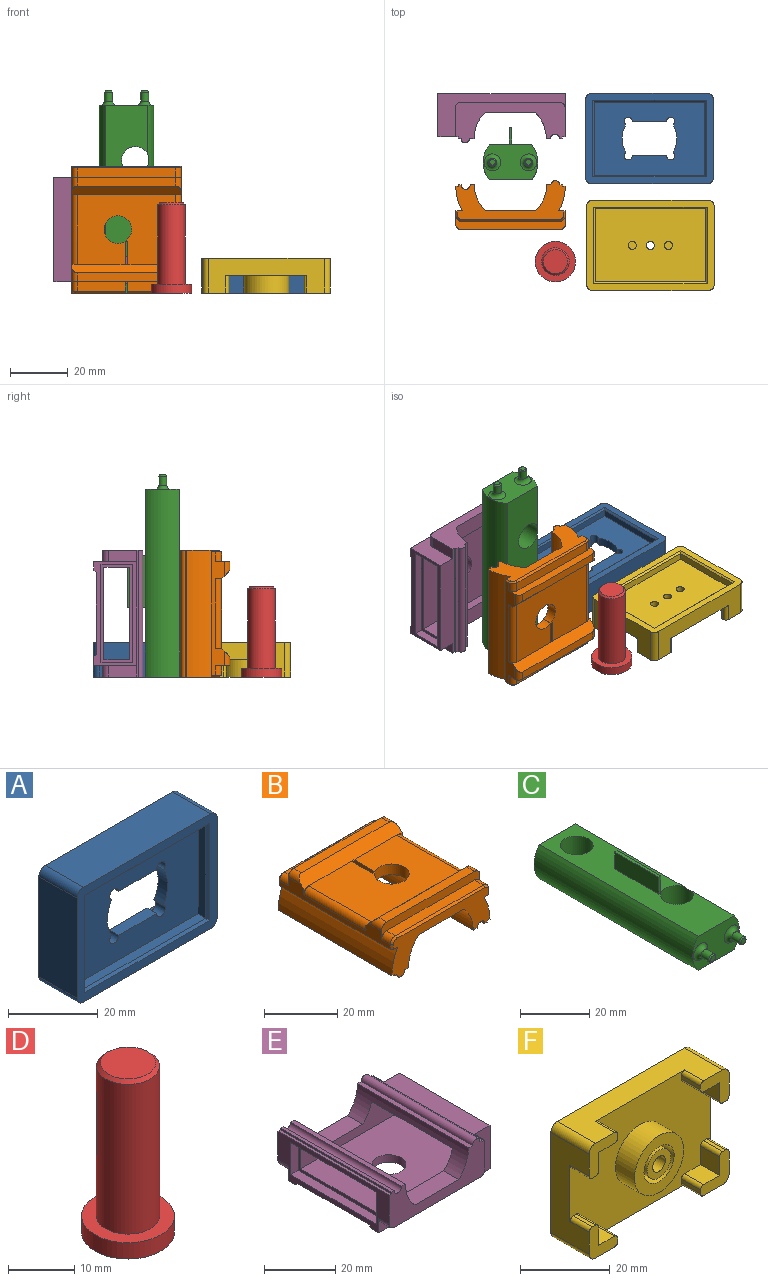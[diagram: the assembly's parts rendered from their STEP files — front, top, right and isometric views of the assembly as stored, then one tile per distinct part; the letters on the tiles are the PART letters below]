
ASSEMBLY  parts=6 mates=5
PART A: 32 faces, bbox 44.1x12x31.3 mm
  f0: plane 38.1x25.3mm, normal (0,1,0), area 736.2mm2, adj f1,f2,f3,f4,f5,f6,f7,f8
  f1: cylinder r=1.4mm len=3mm, axis (0,1,0), area 17.2mm2, adj f0,f2,f8,f9
  f2: plane 11.93x3mm, normal (0,0,-1), area 35.8mm2, adj f0,f1,f3,f9
  f3: cylinder r=1.4mm len=3mm, axis (0,1,0), area 17.2mm2, adj f0,f2,f4,f9
  f4: cylinder r=9.5mm len=9.7mm, axis (0,1,0), area 30.6mm2, adj f0,f3,f5,f9
  f5: cylinder r=1.4mm len=3mm, axis (0,1,0), area 17.2mm2, adj f0,f4,f6,f9
  f6: plane 11.93x3mm, normal (0,0,1), area 35.8mm2, adj f0,f5,f7,f9
  f7: cylinder r=1.4mm len=3mm, axis (0,1,0), area 17.2mm2, adj f0,f6,f8,f9
  f8: cylinder r=9.5mm len=9.7mm, axis (0,1,0), area 30.6mm2, adj f0,f1,f7,f9
  f9: plane 38.1x25.3mm, normal (0,-1,0), area 736.2mm2, adj f1,f2,f3,f4,f5,f6,f7,f8
  f10: plane 38.1x2.4mm, normal (0,0,-1), area 91.4mm2, adj f9,f11,f13,f25
  f11: plane 25.3x2.4mm, normal (1,0,0), area 60.7mm2, adj f9,f10,f12,f24
  f12: plane 38.1x2.4mm, normal (0,0,1), area 91.4mm2, adj f9,f11,f13,f26
  f13: plane 25.3x2.4mm, normal (-1,0,0), area 60.7mm2, adj f9,f10,f12,f27
  f14: plane 40.1x12mm, normal (0,0,1), area 481.2mm2, adj f18,f23,f28,f31
  f15: plane 27.3x12mm, normal (-1,0,0), area 327.6mm2, adj f18,f23,f28,f29
  f16: plane 40.1x12mm, normal (0,0,-1), area 481.2mm2, adj f18,f23,f29,f30
  f17: plane 27.3x12mm, normal (1,0,0), area 327.6mm2, adj f18,f23,f30,f31
  f18: plane 44.1x31.3mm, normal (0,-1,0), area 335.4mm2, adj f14,f15,f16,f17,f24,f25,f26,f27
  f19: plane 25.3x6mm, normal (1,0,0), area 151.8mm2, adj f0,f20,f22,f23
  f20: plane 38.1x6mm, normal (0,0,-1), area 228.6mm2, adj f0,f19,f21,f23
  f21: plane 25.3x6mm, normal (-1,0,0), area 151.8mm2, adj f0,f20,f22,f23
  f22: plane 38.1x6mm, normal (0,0,1), area 228.6mm2, adj f0,f19,f21,f23
  f23: plane 44.1x31.3mm, normal (0,1,0), area 413mm2, adj f14,f15,f16,f17,f19,f20,f21,f22
  f24: plane 26.5x0.6mm, normal (0.71,-0.71,0), area 22mm2, adj f11,f18,f25,f26
  f25: plane 39.3x0.6mm, normal (0,-0.71,-0.71), area 32.8mm2, adj f10,f18,f24,f27
  f26: plane 39.3x0.6mm, normal (0,-0.71,0.71), area 32.8mm2, adj f12,f18,f24,f27
  f27: plane 26.5x0.6mm, normal (-0.71,-0.71,0), area 22mm2, adj f13,f18,f25,f26
  f28: cylinder r=2mm len=12mm, axis (0,-1,0), area 37.7mm2, adj f14,f15,f18,f23
  f29: cylinder r=2mm len=12mm, axis (0,1,0), area 37.7mm2, adj f15,f16,f18,f23
  f30: cylinder r=2mm len=12mm, axis (0,-1,0), area 37.7mm2, adj f16,f17,f18,f23
  f31: cylinder r=2mm len=12mm, axis (0,1,0), area 37.7mm2, adj f14,f17,f18,f23
PART B: 62 faces, bbox 38x44x17 mm
  f0: plane 1.9x1.36mm, normal (0,1,0), area 0.7mm2, adj f18,f42,f61
  f1: plane 1.9x1.36mm, normal (0,-1,0), area 0.7mm2, adj f17,f41,f60
  f2: plane 16.5x3.4mm, normal (0,0,1), area 56.1mm2, adj f4,f36,f40,f49
  f3: plane 16.5x3.4mm, normal (0,0,1), area 56.1mm2, adj f5,f36,f39,f52
  f4: plane 18x3.6mm, normal (1,0,0), area 64.1mm2, adj f2,f6,f8,f30,f31,f35,f36,f49
  f5: plane 17.96x3.6mm, normal (-1,0,0), area 63.9mm2, adj f3,f6,f8,f9,f10,f35,f36,f52
  f6: plane 34x24.21mm, normal (0,0,1), area 744.1mm2, adj f4,f5,f10,f31,f41,f42,f60,f61
  f7: plane 34x3.4mm, normal (0,0,1), area 115.6mm2, adj f34,f47,f48,f57
  f8: plane 44x17.35mm, normal (0,0,-1), area 674.5mm2, adj f4,f5,f9,f10,f26,f27,f29,f30
  f9: plane 18.49x12mm, normal (0,1,0), area 111.8mm2, adj f5,f8,f11,f12,f13,f14,f15,f16
  f10: cylinder r=4.75mm len=9.5mm, axis (0,0,-1), area 107.3mm2, adj f5,f6,f8,f31
  f11: cylinder r=1.5mm len=44mm, axis (0,1,0), area 207.3mm2, adj f9,f12,f28,f29
  f12: plane 44x1mm, normal (0,0,-1), area 44mm2, adj f9,f11,f13,f29
  f13: plane 44x0.5mm, normal (1,0,0), area 22mm2, adj f9,f12,f14,f29
  f14: plane 44x0.99mm, normal (0,0,-1), area 43.7mm2, adj f9,f13,f15,f29
  f15: cylinder r=19mm len=44mm, axis (0,1,0), area 390.5mm2, adj f9,f14,f16,f29
  f16: plane 44x2.27mm, normal (0,0,-1), area 99.4mm2, adj f9,f15,f17,f29,f54,f55
  f17: plane 42.8x4.5mm, normal (1,0,0), area 102.4mm2, adj f1,f16,f32,f34,f36,f39,f41,f44
  f18: plane 42.8x4.5mm, normal (-1,0,0), area 102.4mm2, adj f0,f19,f34,f36,f38,f40,f42,f43
  f19: plane 44x2.27mm, normal (0,0,-1), area 99.4mm2, adj f18,f20,f29,f30,f51,f59
  f20: cylinder r=19mm len=44mm, axis (0,1,0), area 390.5mm2, adj f19,f21,f29,f30
  f21: plane 44x0.99mm, normal (0,0,-1), area 43.7mm2, adj f20,f22,f29,f30
  f22: plane 44x0.5mm, normal (-1,0,0), area 22mm2, adj f21,f23,f29,f30
  f23: plane 44x1mm, normal (0,0,-1), area 44mm2, adj f22,f24,f29,f30
  f24: cylinder r=1.5mm len=44mm, axis (0,1,0), area 207.3mm2, adj f23,f25,f29,f30
  f25: plane 44x1.5mm, normal (0,0,-1), area 66mm2, adj f24,f26,f29,f30
  f26: cylinder r=12.5mm len=44mm, axis (0,1,0), area 442.1mm2, adj f8,f25,f29,f30
  f27: cylinder r=12.5mm len=44mm, axis (0,1,0), area 442.1mm2, adj f8,f9,f28,f29
  f28: plane 44x1.5mm, normal (0,0,-1), area 66mm2, adj f9,f11,f27,f29
  f29: plane 37.99x13.5mm, normal (0,-1,0), area 233.8mm2, adj f8,f11,f12,f13,f14,f15,f16,f19
  f30: plane 18.49x13.5mm, normal (0,1,0), area 118.9mm2, adj f4,f8,f19,f20,f21,f22,f23,f24
  f31: plane 3.6x0.94mm, normal (0,1,0), area 3.4mm2, adj f4,f6,f8,f10
  f32: plane 1.9x1.36mm, normal (0,1,0), area 0.7mm2, adj f17,f41,f61
  f33: plane 34x3mm, normal (0,0,1), area 102mm2, adj f34,f45,f46,f61
  f34: plane 38x4.9mm, normal (0,-1,0), area 110.1mm2, adj f7,f17,f18,f33,f45,f46,f47,f48
  f35: plane 6x1mm, normal (0,0,-1), area 6mm2, adj f4,f5,f36,f60
  f36: plane 38x4.9mm, normal (0,1,0), area 110.2mm2, adj f2,f3,f4,f5,f17,f18,f35,f37
  f37: plane 34x3mm, normal (0,0,1), area 102mm2, adj f36,f43,f44,f60
  f38: plane 1.9x1.36mm, normal (0,-1,0), area 0.7mm2, adj f18,f42,f60
  f39: cylinder r=2mm len=3.4mm, axis (0,1,0), area 10.7mm2, adj f3,f17,f36,f53
  f40: cylinder r=2mm len=3.4mm, axis (0,-1,0), area 10.7mm2, adj f2,f18,f36,f50
  f41: cylinder r=2mm len=24.21mm, axis (0,1,0), area 75.5mm2, adj f1,f6,f17,f32,f60,f61
  f42: cylinder r=2mm len=24.21mm, axis (0,-1,0), area 75.5mm2, adj f0,f6,f18,f38,f60,f61
  f43: cylinder r=2mm len=5mm, axis (0,-1,0), area 11.7mm2, adj f18,f36,f37,f60
  f44: cylinder r=2mm len=5mm, axis (0,1,0), area 11.7mm2, adj f17,f36,f37,f60
  f45: cylinder r=2mm len=5mm, axis (0,-1,0), area 11.7mm2, adj f18,f33,f34,f61
  f46: cylinder r=2mm len=5mm, axis (0,1,0), area 11.7mm2, adj f17,f33,f34,f61
  f47: cylinder r=2mm len=3.4mm, axis (0,-1,0), area 10.7mm2, adj f7,f18,f34,f58
  f48: cylinder r=2mm len=3.4mm, axis (0,1,0), area 10.7mm2, adj f7,f17,f34,f56
  f49: plane 16.5x0.6mm, normal (0,0.71,0.71), area 14mm2, adj f2,f4,f30,f50
  f50: cone r=1.4mm half-angle=45deg, axis (0,-1,0), area 2.3mm2, adj f30,f40,f49,f51
  f51: plane 1.6x0.6mm, normal (-0.71,0.71,0), area 1.4mm2, adj f18,f19,f30,f50
  f52: plane 16.5x0.6mm, normal (0,0.71,0.71), area 14mm2, adj f3,f5,f9,f53
  f53: cone r=1.4mm half-angle=45deg, axis (0,-1,0), area 2.3mm2, adj f9,f39,f52,f54
  f54: plane 1.6x0.6mm, normal (0.71,0.71,0), area 1.4mm2, adj f9,f16,f17,f53
  f55: plane 1.6x0.6mm, normal (0.71,-0.71,0), area 1.4mm2, adj f16,f17,f29,f56
  f56: cone r=1.4mm half-angle=45deg, axis (0,1,0), area 2.3mm2, adj f29,f48,f55,f57
  f57: plane 34x0.6mm, normal (0,-0.71,0.71), area 28.8mm2, adj f7,f29,f56,f58
  f58: cone r=1.4mm half-angle=45deg, axis (0,1,0), area 2.3mm2, adj f29,f47,f57,f59
  f59: plane 1.6x0.6mm, normal (-0.71,-0.71,0), area 1.4mm2, adj f18,f19,f29,f58
  f60: plane 38x3mm, normal (0,-0.71,0.71), area 153.8mm2, adj f1,f4,f5,f6,f17,f18,f35,f37
  f61: plane 38x3mm, normal (0,0.71,0.71), area 153.7mm2, adj f0,f6,f17,f18,f32,f33,f41,f42
PART C: 21 faces, bbox 21.1x70x18 mm
  f0: plane 65x14.73mm, normal (0,0,1), area 798.8mm2, adj f1,f2,f4,f5,f6,f7,f8,f14
  f1: cylinder r=9.5mm len=65mm, axis (0,1,0), area 841.1mm2, adj f0,f3,f4,f5,f14
  f2: cylinder r=9.5mm len=65mm, axis (0,1,0), area 844.2mm2, adj f0,f3,f4,f5
  f3: plane 65x14.73mm, normal (0,0,-1), area 816.7mm2, adj f1,f2,f4,f5,f14,f15
  f4: plane 19x12mm, normal (0,-1,0), area 158.9mm2, adj f0,f1,f2,f3,f19,f20
  f5: plane 19x12mm, normal (0,1,0), area 211.8mm2, adj f0,f1,f2,f3
  f6: plane 6x1mm, normal (0,1,0), area 6mm2, adj f0,f7,f8,f9
  f7: plane 17.96x6mm, normal (-1,0,0), area 107.8mm2, adj f0,f6,f9,f16
  f8: plane 17.96x6mm, normal (1,0,0), area 107.8mm2, adj f0,f6,f9,f16
  f9: plane 17.96x1mm, normal (0,0,1), area 18mm2, adj f6,f7,f8,f16
  f10: cylinder r=1.4mm len=3.1mm, axis (0,1,0), area 27.3mm2, adj f18,f20
  f11: plane 2x2mm, normal (0,-1,0), area 3.1mm2, adj f18
  f12: cylinder r=1.4mm len=3.1mm, axis (0,1,0), area 27.3mm2, adj f17,f19
  f13: plane 2x2mm, normal (0,-1,0), area 3.1mm2, adj f17
  f14: cylinder r=4.75mm len=12mm, axis (0,0,-1), area 355.6mm2, adj f0,f1,f3
  f15: cylinder r=4.75mm len=12mm, axis (0,0,1), area 358.1mm2, adj f0,f3
  f16: plane 6x1mm, normal (0,-1,0), area 6mm2, adj f0,f7,f8,f9
  f17: cone r=1mm half-angle=45deg, axis (0,1,0), area 4.3mm2, adj f12,f13
  f18: cone r=1mm half-angle=45deg, axis (0,1,0), area 4.3mm2, adj f10,f11
  f19: torus R=2.9mm, axis (0,-1,0), area 28.8mm2, adj f4,f12
  f20: torus R=2.9mm, axis (0,-1,0), area 28.8mm2, adj f4,f10
PART D: 6 faces, bbox 14x14x31.2 mm
  f0: cylinder r=4.75mm len=27.6mm, axis (0,0,-1), area 823.7mm2, adj f3,f5
  f1: plane 8.3x8.3mm, normal (0,0,1), area 54.1mm2, adj f5
  f2: cylinder r=7mm len=14mm, axis (0,0,-1), area 131.9mm2, adj f3,f4
  f3: plane 14x14mm, normal (0,0,1), area 83.1mm2, adj f0,f2
  f4: plane 14x14mm, normal (0,0,-1), area 153.9mm2, adj f2
  f5: cone r=4.15mm half-angle=45deg, axis (0,0,-1), area 23.7mm2, adj f0,f1
PART E: 49 faces, bbox 44x44x17 mm
  f0: plane 38x14mm, normal (0,1,0), area 268.4mm2, adj f3,f5,f11,f12,f13,f17,f18,f19
  f1: plane 38x14mm, normal (0,-1,0), area 268.4mm2, adj f3,f4,f5,f11,f12,f16,f17,f18
  f2: plane 36x14.9mm, normal (1,0,0), area 136.3mm2, adj f3,f15,f26,f27,f28,f29,f30,f31
  f3: plane 44x7mm, normal (0,0,1), area 260mm2, adj f0,f1,f2,f22,f26,f28,f43,f44
  f4: plane 34x4mm, normal (0,0,-1), area 136mm2, adj f1,f28,f46,f48
  f5: plane 44x14.9mm, normal (-1,0,0), area 215.5mm2, adj f0,f1,f15,f21,f26,f27,f28,f29
  f6: plane 38x9mm, normal (0,1,0), area 212.6mm2, adj f8,f9,f10,f11,f12,f16,f34,f39
  f7: plane 38x9mm, normal (0,-1,0), area 212.6mm2, adj f8,f9,f10,f11,f12,f13,f34,f39
  f8: plane 38x32mm, normal (0,0,1), area 1145.1mm2, adj f6,f7,f14,f34,f39
  f9: plane 32x3.87mm, normal (0,0,-1), area 123.7mm2, adj f6,f7,f12,f39
  f10: plane 32x9.87mm, normal (0,0,-1), area 315.7mm2, adj f6,f7,f11,f34
  f11: cylinder r=12.5mm len=44mm, axis (0,1,0), area 217.5mm2, adj f0,f1,f6,f7,f10,f13,f16,f25
  f12: cylinder r=12.5mm len=44mm, axis (0,1,0), area 217.5mm2, adj f0,f1,f6,f7,f9,f13,f16,f17
  f13: plane 17.35x6mm, normal (0,0,1), area 104.1mm2, adj f0,f7,f11,f12
  f14: cylinder r=4.75mm len=9.5mm, axis (0,0,1), area 77.7mm2, adj f8,f15
  f15: plane 44x28.21mm, normal (0,0,-1), area 1170.2mm2, adj f2,f5,f14,f41,f42
  f16: plane 17.35x6mm, normal (0,0,1), area 104.1mm2, adj f1,f6,f11,f12
  f17: plane 44x1.5mm, normal (0,0,1), area 66mm2, adj f0,f1,f12,f18
  f18: cylinder r=1.5mm len=44mm, axis (0,1,0), area 207.3mm2, adj f0,f1,f17,f19
  f19: plane 44x1mm, normal (0,0,1), area 44mm2, adj f0,f1,f18,f20
  f20: plane 44x0.6mm, normal (-1,0,0), area 26.4mm2, adj f0,f1,f19,f21
  f21: plane 44x1mm, normal (0,0,1), area 44mm2, adj f0,f1,f5,f20
  f22: plane 44x0.6mm, normal (1,0,0), area 26.4mm2, adj f0,f1,f3,f23
  f23: plane 44x1mm, normal (0,0,1), area 44mm2, adj f0,f1,f22,f24
  f24: cylinder r=1.5mm len=44mm, axis (0,1,0), area 207.3mm2, adj f0,f1,f23,f25
  f25: plane 44x1.5mm, normal (0,0,1), area 66mm2, adj f0,f1,f11,f24
  f26: plane 44x14.9mm, normal (0,1,0), area 205.1mm2, adj f2,f3,f5,f27,f40,f44,f45,f47
  f27: plane 44x3mm, normal (0,0,-1), area 132mm2, adj f2,f5,f26,f42
  f28: plane 44x14.9mm, normal (0,-1,0), area 205.1mm2, adj f2,f3,f4,f5,f29,f43,f46,f48
  f29: plane 44x3mm, normal (0,0,-1), area 132mm2, adj f2,f5,f28,f41
  f30: plane 11x3mm, normal (0,1,0), area 33mm2, adj f2,f31,f33,f34
  f31: plane 34x3mm, normal (0,0,1), area 102mm2, adj f2,f30,f32,f34
  f32: plane 11x3mm, normal (0,-1,0), area 33mm2, adj f2,f31,f33,f34
  f33: plane 34x3mm, normal (0,0,-1), area 102mm2, adj f2,f30,f32,f34
  f34: plane 34x11mm, normal (1,0,0), area 86mm2, adj f6,f7,f8,f10,f30,f31,f32,f33
  f35: plane 11x3mm, normal (0,-1,0), area 33mm2, adj f5,f36,f38,f39
  f36: plane 34x3mm, normal (0,0,1), area 102mm2, adj f5,f35,f37,f39
  f37: plane 11x3mm, normal (0,1,0), area 33mm2, adj f5,f36,f38,f39
  f38: plane 34x3mm, normal (0,0,-1), area 102mm2, adj f5,f35,f37,f39
  f39: plane 34x11mm, normal (-1,0,0), area 86mm2, adj f6,f7,f8,f9,f35,f36,f37,f38
  f40: plane 34x4mm, normal (0,0,-1), area 136mm2, adj f0,f26,f45,f47
  f41: plane 44x0.9mm, normal (0,0.71,-0.71), area 55.8mm2, adj f2,f5,f15,f29
  f42: plane 44x0.9mm, normal (0,-0.71,-0.71), area 55.8mm2, adj f2,f5,f15,f27
  f43: plane 9.9x4mm, normal (1,0,0), area 39.6mm2, adj f1,f3,f28,f46
  f44: plane 9.9x4mm, normal (1,0,0), area 39.6mm2, adj f0,f3,f26,f45
  f45: cylinder r=2mm len=4mm, axis (0,-1,0), area 12.6mm2, adj f0,f26,f40,f44
  f46: cylinder r=2mm len=4mm, axis (0,-1,0), area 12.6mm2, adj f1,f4,f28,f43
  f47: cylinder r=2mm len=4mm, axis (0,-1,0), area 12.6mm2, adj f0,f5,f26,f40
  f48: cylinder r=2mm len=4mm, axis (0,-1,0), area 12.6mm2, adj f1,f4,f5,f28
PART F: 69 faces, bbox 44.1x12x31.3 mm
  f0: plane 9.5x9.5mm, normal (0,-1,0), area 26.7mm2, adj f17,f39
  f1: plane 44.1x31.3mm, normal (0,-1,0), area 1015.1mm2, adj f10,f11,f12,f13,f19,f20,f21,f22
  f2: cylinder r=1.4mm len=2.8mm, axis (0,-1,0), area 17.6mm2, adj f5,f16
  f3: cylinder r=1.4mm len=2.8mm, axis (0,-1,0), area 17.6mm2, adj f5,f15
  f4: cylinder r=2mm len=6mm, axis (0,-1,0), area 75.4mm2, adj f18,f47
  f5: plane 38.1x25.3mm, normal (0,1,0), area 945.5mm2, adj f2,f3,f6,f7,f8,f9,f46
  f6: plane 25.3x2.4mm, normal (-1,0,0), area 60.7mm2, adj f5,f7,f9,f44
  f7: plane 38.1x2.4mm, normal (0,0,-1), area 91.4mm2, adj f5,f6,f8,f42
  f8: plane 25.3x2.4mm, normal (1,0,0), area 60.7mm2, adj f5,f7,f9,f43
  f9: plane 38.1x2.4mm, normal (0,0,1), area 91.4mm2, adj f5,f6,f8,f45
  f10: plane 27.3x12mm, normal (-1,0,0), area 235.8mm2, adj f1,f14,f28,f33,f48,f50,f58,f68
  f11: plane 40.1x12mm, normal (0,0,-1), area 312.6mm2, adj f1,f14,f33,f38,f50,f51,f55,f57
  f12: plane 27.3x12mm, normal (1,0,0), area 235.8mm2, adj f1,f14,f23,f38,f49,f51,f54,f64
  f13: plane 40.1x12mm, normal (0,0,1), area 312.6mm2, adj f1,f14,f23,f28,f48,f49,f61,f65
  f14: plane 44.1x31.3mm, normal (0,1,0), area 335.4mm2, adj f10,f11,f12,f13,f42,f43,f44,f45
  f15: plane 2.8x2.8mm, normal (0,1,0), area 6.2mm2, adj f3
  f16: plane 2.8x2.8mm, normal (0,1,0), area 6.2mm2, adj f2
  f17: cylinder r=3.75mm len=7.5mm, axis (0,1,0), area 141.4mm2, adj f0,f18
  f18: plane 7.5x7.5mm, normal (0,-1,0), area 31.6mm2, adj f4,f17
  f19: plane 6x1mm, normal (-1,0,0), area 6mm2, adj f1,f23,f61,f62
  f20: plane 6x5mm, normal (0,0,-1), area 30mm2, adj f1,f21,f23,f62
  f21: plane 6x5mm, normal (-1,0,0), area 30mm2, adj f1,f20,f23,f63
  f22: plane 6x1mm, normal (0,0,-1), area 6mm2, adj f1,f23,f63,f64
  f23: plane 9x9mm, normal (0,-1,0), area 43.3mm2, adj f12,f13,f19,f20,f21,f22,f49,f61
  f24: plane 6x1mm, normal (0,0,-1), area 6mm2, adj f1,f28,f67,f68
  f25: plane 6x5mm, normal (1,0,0), area 30mm2, adj f1,f26,f28,f67
  f26: plane 6x5mm, normal (0,0,-1), area 30mm2, adj f1,f25,f28,f66
  f27: plane 6x1mm, normal (1,0,0), area 6mm2, adj f1,f28,f65,f66
  f28: plane 9x9mm, normal (0,-1,0), area 43.3mm2, adj f10,f13,f24,f25,f26,f27,f48,f65
  f29: plane 6x1mm, normal (1,0,0), area 6mm2, adj f1,f33,f57,f60
  f30: plane 6x5mm, normal (0,0,1), area 30mm2, adj f1,f31,f33,f60
  f31: plane 6x5mm, normal (1,0,0), area 30mm2, adj f1,f30,f33,f59
  f32: plane 6x1mm, normal (0,0,1), area 6mm2, adj f1,f33,f58,f59
  f33: plane 9x9mm, normal (0,-1,0), area 43.3mm2, adj f10,f11,f29,f30,f31,f32,f50,f57
  f34: plane 6x5mm, normal (0,0,1), area 30mm2, adj f1,f37,f38,f56
  f35: plane 6x1mm, normal (-1,0,0), area 6mm2, adj f1,f38,f55,f56
  f36: plane 6x1mm, normal (0,0,1), area 6mm2, adj f1,f38,f53,f54
  f37: plane 6x5mm, normal (-1,0,0), area 30mm2, adj f1,f34,f38,f53
  f38: plane 9x9mm, normal (0,-1,0), area 43.3mm2, adj f11,f12,f34,f35,f36,f37,f51,f53
  f39: cylinder r=4.75mm len=9.5mm, axis (0,1,0), area 179.1mm2, adj f0,f41
  f40: cylinder r=7.75mm len=15.5mm, axis (0,1,0), area 292.2mm2, adj f1,f41
  f41: plane 15.5x15.5mm, normal (0,-1,0), area 117.8mm2, adj f39,f40
  f42: plane 39.3x0.6mm, normal (0,0.71,-0.71), area 32.8mm2, adj f7,f14,f43,f44
  f43: plane 26.5x0.6mm, normal (0.71,0.71,0), area 22mm2, adj f8,f14,f42,f45
  f44: plane 26.5x0.6mm, normal (-0.71,0.71,0), area 22mm2, adj f6,f14,f42,f45
  f45: plane 39.3x0.6mm, normal (0,0.71,0.71), area 32.8mm2, adj f9,f14,f43,f44
  f46: cylinder r=1.4mm len=2.8mm, axis (0,-1,0), area 22.9mm2, adj f5,f52
  f47: plane 4x4mm, normal (0,-1,0), area 2.4mm2, adj f4,f52
  f48: cylinder r=2mm len=12mm, axis (0,1,0), area 37.7mm2, adj f10,f13,f14,f28
  f49: cylinder r=2mm len=12mm, axis (0,-1,0), area 37.7mm2, adj f12,f13,f14,f23
  f50: cylinder r=2mm len=12mm, axis (0,-1,0), area 37.7mm2, adj f10,f11,f14,f33
  f51: cylinder r=2mm len=12mm, axis (0,1,0), area 37.7mm2, adj f11,f12,f14,f38
  f52: cone r=1.4mm half-angle=45deg, axis (0,-1,0), area 5.7mm2, adj f46,f47
  f53: cylinder r=1mm len=6mm, axis (0,-1,0), area 9.4mm2, adj f1,f36,f37,f38
  f54: cylinder r=1mm len=6mm, axis (0,-1,0), area 9.4mm2, adj f1,f12,f36,f38
  f55: cylinder r=1mm len=6mm, axis (0,-1,0), area 9.4mm2, adj f1,f11,f35,f38
  f56: cylinder r=1mm len=6mm, axis (0,-1,0), area 9.4mm2, adj f1,f34,f35,f38
  f57: cylinder r=1mm len=6mm, axis (0,1,0), area 9.4mm2, adj f1,f11,f29,f33
  f58: cylinder r=1mm len=6mm, axis (0,1,0), area 9.4mm2, adj f1,f10,f32,f33
  f59: cylinder r=1mm len=6mm, axis (0,1,0), area 9.4mm2, adj f1,f31,f32,f33
  f60: cylinder r=1mm len=6mm, axis (0,1,0), area 9.4mm2, adj f1,f29,f30,f33
  f61: cylinder r=1mm len=6mm, axis (0,1,0), area 9.4mm2, adj f1,f13,f19,f23
  f62: cylinder r=1mm len=6mm, axis (0,1,0), area 9.4mm2, adj f1,f19,f20,f23
  f63: cylinder r=1mm len=6mm, axis (0,1,0), area 9.4mm2, adj f1,f21,f22,f23
  f64: cylinder r=1mm len=6mm, axis (0,1,0), area 9.4mm2, adj f1,f12,f22,f23
  f65: cylinder r=1mm len=6mm, axis (0,-1,0), area 9.4mm2, adj f1,f13,f27,f28
  f66: cylinder r=1mm len=6mm, axis (0,-1,0), area 9.4mm2, adj f1,f26,f27,f28
  f67: cylinder r=1mm len=6mm, axis (0,-1,0), area 9.4mm2, adj f1,f24,f25,f28
  f68: cylinder r=1mm len=6mm, axis (0,-1,0), area 9.4mm2, adj f1,f10,f24,f28
PLACE A rot(axis=(-1,0,0),90deg) t=(47.88,8.3,-14)mm
PLACE B rot(axis=(0,-0.71,0.71),180deg) t=(-0.22,-7.81,2)mm
PLACE C rot(axis=(-1,0,0),90deg) t=(-0.22,0,26)mm fixed
PLACE D t=(15.31,-34.29,-20)mm
PLACE E rot(axis=(0,0.71,-0.71),180deg) t=(-0.34,8.34,2)mm
PLACE F rot(axis=(1,0,0),90deg) t=(48.19,-28.65,-14)mm
MATE planar C.f1 <-> A.f4  axis (0,0,-1) through (-0.22,0,-20)mm
MATE planar C.f1 <-> B.f27  axis (0,0,-1) through (-0.22,0,-20)mm
MATE planar C.f1 <-> E.f0  axis (0,0,-1) through (-0.22,0,-20)mm
MATE planar C.f1 <-> F.f17  axis (0,0,-1) through (-0.22,0,-20)mm
MATE planar C.f5 <-> D.f2  axis (0,0,-1) through (-0.22,-6,-20)mm
